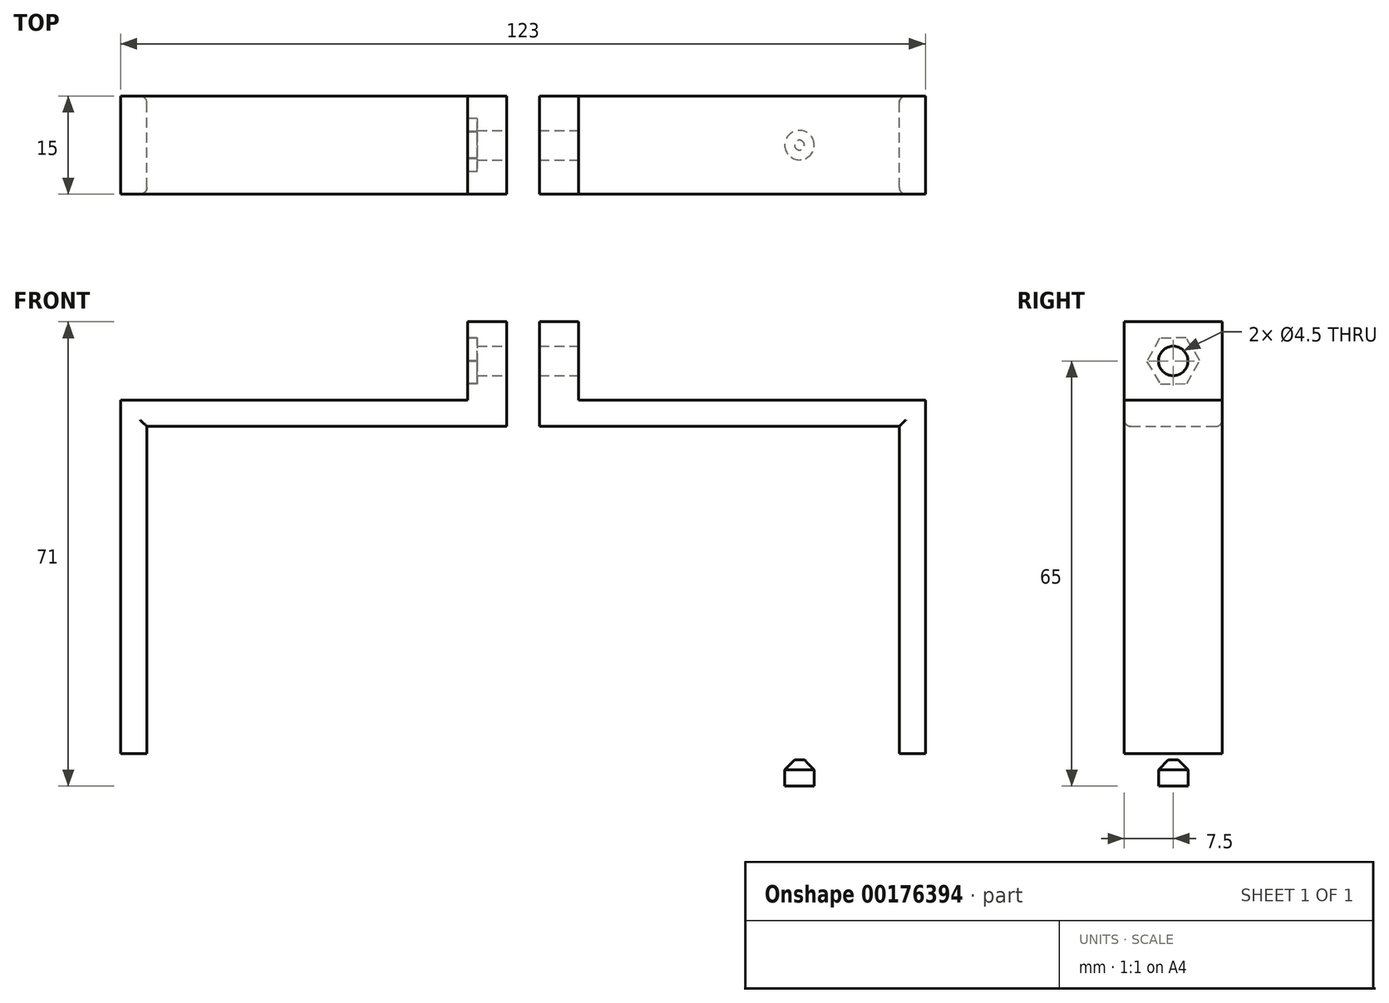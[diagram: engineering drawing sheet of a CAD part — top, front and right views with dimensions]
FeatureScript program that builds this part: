
annotation { "Feature Type Name" : "Feature", "Feature Type Description" : "" }
export const myFeature = defineFeature(function(context is Context, id is Id, definition is map)
    precondition{}
    {
        {
            var Q0;
            Q0=qCreatedBy(makeId("Front.planeOp"),FACE);
            var sketch = newSketch(context, id + "F0", { "sketchPlane" : qUnion([Q0])});
            skLineSegment(sketch, "E0.bottom", {"start": v(-57.5, 25.5) * mm, "end": v(-2.5, 25.5) * mm});
            skLineSegment(sketch, "E0.top", {"start": v(-57.5, -25.5) * mm, "end": v(57.5, -25.5) * mm});
            skLineSegment(sketch, "E0.left", {"start": v(-57.5, 25.5) * mm, "end": v(-57.5, -25.5) * mm});
            skLineSegment(sketch, "E0.right", {"start": v(57.5, 25.5) * mm, "end": v(57.5, -25.5) * mm});
            skLineSegment(sketch, "E1.bottom", {"start": v(-61.5, 29.5) * mm, "end": v(-8.5, 29.5) * mm});
            skLineSegment(sketch, "E1.top", {"start": v(-61.5, -29.5) * mm, "end": v(61.5, -29.5) * mm});
            skLineSegment(sketch, "E1.left", {"start": v(-61.5, 29.5) * mm, "end": v(-61.5, -29.5) * mm});
            skLineSegment(sketch, "E1.right", {"start": v(61.5, 29.5) * mm, "end": v(61.5, -29.5) * mm});
            skLineSegment(sketch, "E2.bottom", {"start": v(-2.5, 41.5) * mm, "end": v(-8.5, 41.5) * mm});
            skLineSegment(sketch, "E2.top", {"start": v(-2.5, 25.5) * mm, "end": v(-8.5, 25.5) * mm});
            skLineSegment(sketch, "E2.left", {"start": v(-2.5, 41.5) * mm, "end": v(-2.5, 25.5) * mm});
            skLineSegment(sketch, "E2.right", {"start": v(-8.5, 41.5) * mm, "end": v(-8.5, 29.5) * mm});
            skPoint(sketch, "E3.oppositeSnap0", {"position": v(-5.5, 41.5) * mm});
            skLineSegment(sketch, "E3.bottom", {"start": v(2.5, 25.5) * mm, "end": v(8.5, 25.5) * mm});
            skLineSegment(sketch, "E3.top", {"start": v(2.5, 41.5) * mm, "end": v(8.5, 41.5) * mm});
            skLineSegment(sketch, "E3.left", {"start": v(2.5, 25.5) * mm, "end": v(2.5, 41.5) * mm});
            skLineSegment(sketch, "E3.right", {"start": v(8.5, 29.5) * mm, "end": v(8.5, 41.5) * mm});
            skLineSegment(sketch, "E4.trimOffspring", {"start": v(8.5, 29.5) * mm, "end": v(61.5, 29.5) * mm});
            skLineSegment(sketch, "E5.trimOffspring", {"start": v(2.5, 25.5) * mm, "end": v(57.5, 25.5) * mm});
            skSolve(sketch);
        }
        {
            var Q0;
            Q0=makeQuery(id+"F0.imprint","IMPRINT",FACE,{"disambiguationData":[TD([[makeQuery(id+"F0.imprint","IMPRINT",EDGE,{"derivedFrom":sQuery(id+"F0.wireOp",EDGE,"E0.bottom")}),1.0]])]});
            extrude(context, id + "F1", {"entities" : qUnion([Q0]), "depth" : 15 * mm});
        }
        {
            var Q0;
            Q0=makeQuery(id+"F1.opExtrude","SWEPT_FACE",FACE,{"disambiguationData":[OSD([sQuery(id+"F0.wireOp",EDGE,"E3.right")])]});
            var sketch = newSketch(context, id + "F2", { "sketchPlane" : qUnion([Q0])});
            skCircle(sketch, "E6", {"center": v(-7.5, 35.5) * mm, "radius": 2.25 * mm});
            skPoint(sketch, "E6.centerSnap0", {"position": v(-15, 35.5) * mm});
            skPoint(sketch, "E6.centerSnap1", {"position": v(-7.5, 41.5) * mm});
            skSolve(sketch);
        }
        {
            var Q0;
            Q0=makeQuery(id+"F2.imprint","IMPRINT",FACE,{"disambiguationData":[TD([[makeQuery(id+"F2.imprint","IMPRINT",EDGE,{"derivedFrom":sQuery(id+"F2.wireOp",EDGE,"E6")}),1.0]])]});
            extrude(context, id + "F3", {"entities" : qUnion([Q0]), "operationType" : NewBodyOperationType.REMOVE, "oppositeDirection" : true, "depth" : 25 * mm});
        }
        {
            var Q0;
            Q0=makeQuery(id+"F1.opExtrude","SWEPT_FACE",FACE,{"disambiguationData":[OSD([sQuery(id+"F0.wireOp",EDGE,"E1.top")])]});
            var sketch = newSketch(context, id + "F4", { "sketchPlane" : qUnion([Q0])});
            skCircle(sketch, "E7", {"center": v(-42.25, 7.5) * mm, "radius": 2.25 * mm});
            skPoint(sketch, "E7.centerSnap0", {"position": v(-61.5, 7.5) * mm});
            skCircle(sketch, "E8.MirrorC", {"center": v(42.25, 7.5) * mm, "radius": 2.25 * mm});
            skSolve(sketch);
        }
        {
            var Q0;
            Q0=makeQuery(id+"F4.imprint","IMPRINT",FACE,{"disambiguationData":[TD([[makeQuery(id+"F4.imprint","IMPRINT",EDGE,{"derivedFrom":sQuery(id+"F4.wireOp",EDGE,"E7")}),1.0]])]});
            var Q1;
            Q1=makeQuery(id+"F4.imprint","IMPRINT",FACE,{"disambiguationData":[TD([[makeQuery(id+"F4.imprint","IMPRINT",EDGE,{"derivedFrom":sQuery(id+"F4.wireOp",EDGE,"E8.MirrorC")}),-1.0]])]});
            extrude(context, id + "F5", {"entities" : qUnion([Q0, Q1]), "operationType" : NewBodyOperationType.REMOVE, "oppositeDirection" : true, "depth" : 5 * mm});
        }
        {
            var Q0;
            Q0=makeQuery(id+"F5.boolean.opBoolean","INTERSECT",EDGE,{"derivedFrom":[makeQuery(id+"F1.opExtrude","SWEPT_FACE",FACE,{"disambiguationData":[OSD([sQuery(id+"F0.wireOp",EDGE,"E0.top")])]}),makeQuery(id+"F5.opExtrude","SWEPT_FACE",FACE,{"disambiguationData":[OSD([sQuery(id+"F4.wireOp",EDGE,"E7")])]})]});
            var Q1;
            Q1=makeQuery(id+"F5.boolean.opBoolean","INTERSECT",EDGE,{"derivedFrom":[makeQuery(id+"F1.opExtrude","SWEPT_FACE",FACE,{"disambiguationData":[OSD([sQuery(id+"F0.wireOp",EDGE,"E0.top")])]}),makeQuery(id+"F5.opExtrude","SWEPT_FACE",FACE,{"disambiguationData":[OSD([sQuery(id+"F4.wireOp",EDGE,"E8.MirrorC")])]})]});
            chamfer(context, id + "F6", {"entities" : qUnion([Q0, Q1]), "width" : 1.5 * mm, "tangentPropagation" : true});
        }
        {
            var Q0;
            Q0=makeQuery(id+"F1.opExtrude","SWEPT_FACE",FACE,{"disambiguationData":[OSD([sQuery(id+"F0.wireOp",EDGE,"E2.right")])]});
            var sketch = newSketch(context, id + "F7", { "sketchPlane" : qUnion([Q0])});
            skCircle(sketch, "E9.cCircle", {"center": v(7.5, 35.5) * mm, "radius": 3.5 * mm, "construction": true});
            skLineSegment(sketch, "E9.0", {"start": v(11.54, 35.43) * mm, "end": v(9.46, 31.96) * mm});
            skLineSegment(sketch, "E9.1", {"start": v(9.46, 31.96) * mm, "end": v(5.42, 32.04) * mm});
            skLineSegment(sketch, "E9.2", {"start": v(5.42, 32.04) * mm, "end": v(3.46, 35.57) * mm});
            skLineSegment(sketch, "E9.3", {"start": v(3.46, 35.57) * mm, "end": v(5.54, 39.04) * mm});
            skLineSegment(sketch, "E9.4", {"start": v(5.54, 39.04) * mm, "end": v(9.58, 38.96) * mm});
            skLineSegment(sketch, "E9.5", {"start": v(9.58, 38.96) * mm, "end": v(11.54, 35.43) * mm});
            skPoint(sketch, "E9.0.midPoint", {"position": v(10.5, 33.7) * mm});
            skSolve(sketch);
        }
        {
            var Q0;
            Q0=makeQuery(id+"F7.imprint","IMPRINT",FACE,{"disambiguationData":[TD([[makeQuery(id+"F7.imprint","IMPRINT",EDGE,{"derivedFrom":sQuery(id+"F7.wireOp",EDGE,"E9.0")}),-1.0]])]});
            extrude(context, id + "F8", {"entities" : qUnion([Q0]), "operationType" : NewBodyOperationType.REMOVE, "oppositeDirection" : true, "depth" : 1.5 * mm});
        }
        {
            var Q0;
            Q0=makeQuery(id+"F1.opExtrude","CAP_EDGE",EDGE,{"disambiguationData":[OSD([sQuery(id+"F0.wireOp",EDGE,"E5.trimOffspring")])],"isStart":true});
            var Q1;
            Q1=makeQuery(id+"F1.opExtrude","CAP_EDGE",EDGE,{"disambiguationData":[OSD([sQuery(id+"F0.wireOp",EDGE,"E0.right")])],"isStart":true});
            var Q2;
            Q2=makeQuery(id+"F1.opExtrude","CAP_EDGE",EDGE,{"disambiguationData":[OSD([sQuery(id+"F0.wireOp",EDGE,"E0.bottom"),sQuery(id+"F0.wireOp",EDGE,"E2.top")])],"isStart":true});
            var Q3;
            Q3=makeQuery(id+"F1.opExtrude","CAP_EDGE",EDGE,{"disambiguationData":[OSD([sQuery(id+"F0.wireOp",EDGE,"E0.left")])],"isStart":true});
            var Q4;
            Q4=makeQuery(id+"F1.opExtrude","CAP_EDGE",EDGE,{"disambiguationData":[OSD([sQuery(id+"F0.wireOp",EDGE,"E0.top")])],"isStart":true});
            var Q5;
            Q5=makeQuery(id+"F1.opExtrude","CAP_EDGE",EDGE,{"disambiguationData":[OSD([sQuery(id+"F0.wireOp",EDGE,"E0.bottom"),sQuery(id+"F0.wireOp",EDGE,"E2.top")])],"isStart":false});
            var Q6;
            Q6=makeQuery(id+"F1.opExtrude","CAP_EDGE",EDGE,{"disambiguationData":[OSD([sQuery(id+"F0.wireOp",EDGE,"E5.trimOffspring")])],"isStart":false});
            var Q7;
            Q7=makeQuery(id+"F1.opExtrude","CAP_EDGE",EDGE,{"disambiguationData":[OSD([sQuery(id+"F0.wireOp",EDGE,"E0.left")])],"isStart":false});
            var Q8;
            Q8=makeQuery(id+"F1.opExtrude","CAP_EDGE",EDGE,{"disambiguationData":[OSD([sQuery(id+"F0.wireOp",EDGE,"E0.top")])],"isStart":false});
            var Q9;
            Q9=makeQuery(id+"F1.opExtrude","CAP_EDGE",EDGE,{"disambiguationData":[OSD([sQuery(id+"F0.wireOp",EDGE,"E0.right")])],"isStart":false});
            fillet(context, id + "F9", {"entities" : qUnion([Q0, Q1, Q2, Q3, Q4, Q5, Q6, Q7, Q8, Q9]), "radius" : 1 * mm, "tangentPropagation" : true, "allowEdgeOverflow" : false});
        }
    });
